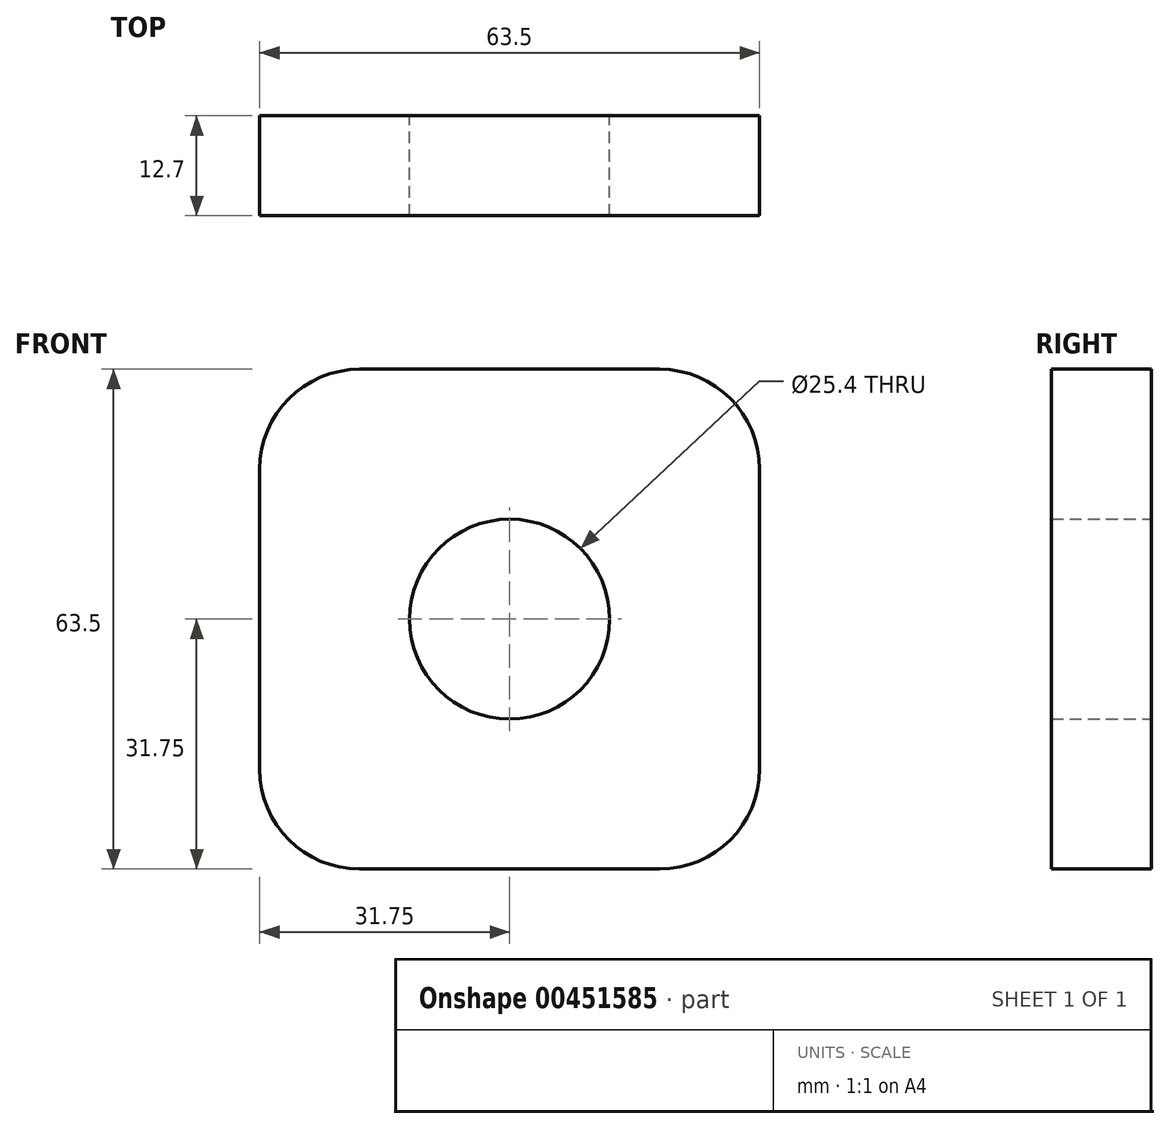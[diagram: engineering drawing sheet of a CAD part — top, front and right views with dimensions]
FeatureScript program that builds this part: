
annotation { "Feature Type Name" : "Feature", "Feature Type Description" : "" }
export const myFeature = defineFeature(function(context is Context, id is Id, definition is map)
    precondition{}
    {
        {
            var Q0;
            Q0=qCreatedBy(makeId("Front.planeOp"),FACE);
            var sketch = newSketch(context, id + "F0", { "sketchPlane" : qUnion([Q0])});
            skCircle(sketch, "E0", {"center": v(0, 0) * mm, "radius": 12.7 * mm});
            skLineSegment(sketch, "E1.bottom", {"start": v(19.05, 31.75) * mm, "end": v(-19.05, 31.75) * mm});
            skLineSegment(sketch, "E1.top", {"start": v(19.05, -31.75) * mm, "end": v(-19.05, -31.75) * mm});
            skLineSegment(sketch, "E1.left", {"start": v(31.75, 19.05) * mm, "end": v(31.75, -19.05) * mm});
            skLineSegment(sketch, "E1.right", {"start": v(-31.75, 19.05) * mm, "end": v(-31.75, -19.05) * mm});
            skPoint(sketch, "E2.visualSharp", {"position": v(-31.75, 31.75) * mm});
            skArc(sketch, "E2.filletArc", {"start": v(-19.05, 31.75) * mm, "mid": v(-28.03, 28.03) * mm, "end": v(-31.75, 19.05) * mm});
            skPoint(sketch, "E3.visualSharp", {"position": v(31.75, 31.75) * mm});
            skArc(sketch, "E3.filletArc", {"start": v(31.75, 19.05) * mm, "mid": v(28.03, 28.03) * mm, "end": v(19.05, 31.75) * mm});
            skPoint(sketch, "E4.visualSharp", {"position": v(31.75, -31.75) * mm});
            skArc(sketch, "E4.filletArc", {"start": v(19.05, -31.75) * mm, "mid": v(28.03, -28.03) * mm, "end": v(31.75, -19.05) * mm});
            skPoint(sketch, "E5.visualSharp", {"position": v(-31.75, -31.75) * mm});
            skArc(sketch, "E5.filletArc", {"start": v(-31.75, -19.05) * mm, "mid": v(-28.03, -28.03) * mm, "end": v(-19.05, -31.75) * mm});
            skSolve(sketch);
        }
        {
            var Q0;
            Q0 = qSketchRegion(id + "F0", true);
            extrude(context, id + "F1", {"entities" : qUnion([Q0]), "depth" : 12.7 * mm});
        }
    });
